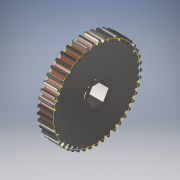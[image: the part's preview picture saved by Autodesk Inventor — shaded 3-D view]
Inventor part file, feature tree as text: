
AUTODESK INVENTOR PART (.ipt)
format: ipt  version: 2018 (Build 220112000, 112)  size: 322,048 bytes
history: native  units: in
note: dims shown in document units (in); Inventor stores cm internally (conversion verified against a paired STEP export)
features: other x3, sketch x1
ambient origin geometry x8: Origin, YZ Plane, XZ Plane, XY Plane, X Axis, Y Axis, Z Axis, Center Point
bodies: Solid1 (feature_tree)
feature tree (4):
  sketch  "Sketch1"  dims[d0=2.25in d1=1.0in d2=0.0in]
  other  "Srf1"
  other  "Cut-Extrude1"
  other  "pitch circle"
